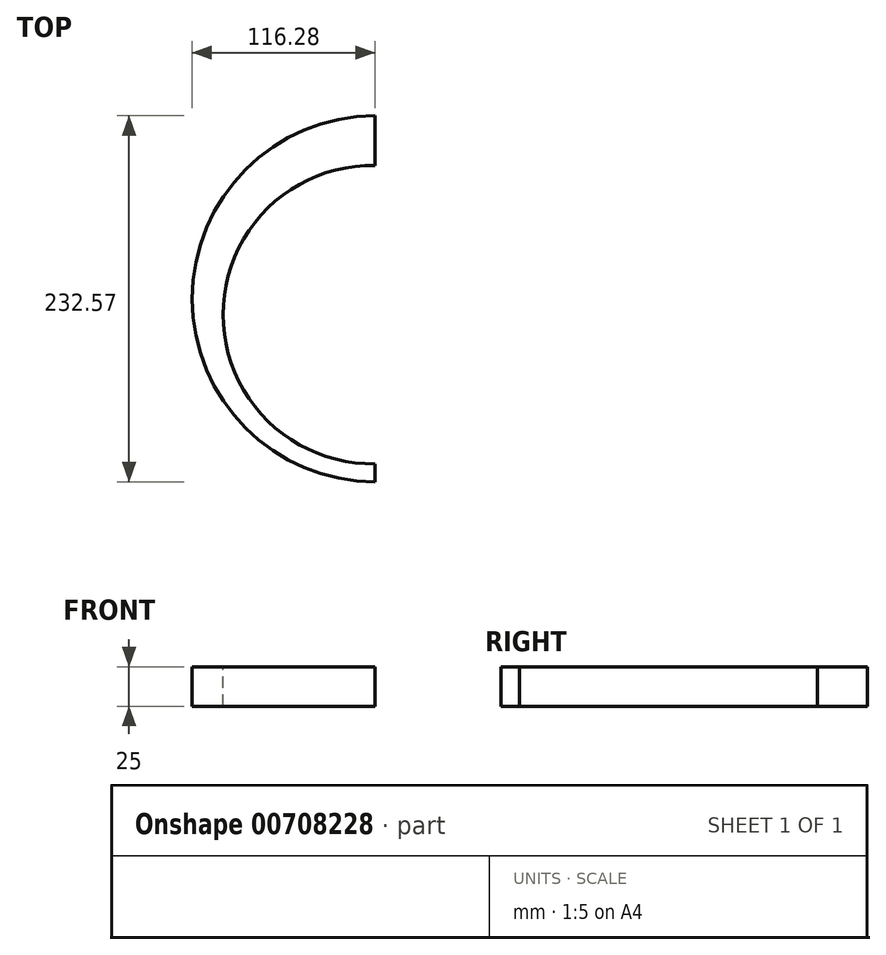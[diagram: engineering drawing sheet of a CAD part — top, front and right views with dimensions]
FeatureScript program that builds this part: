
annotation { "Feature Type Name" : "Feature", "Feature Type Description" : "" }
export const myFeature = defineFeature(function(context is Context, id is Id, definition is map)
    precondition{}
    {
        {
            var Q0;
            Q0=qCreatedBy(makeId("Top.planeOp"),FACE);
            var sketch = newSketch(context, id + "F0", { "sketchPlane" : qUnion([Q0])});
            skCircle(sketch, "E0", {"center": v(-180.25, -20.23) * mm, "radius": 116.29 * mm});
            skSolve(sketch);
        }
        {
            var Q0;
            Q0 = qSketchRegion(id + "F0", true);
            extrude(context, id + "F1", {"entities" : qUnion([Q0]), "depth" : 25 * mm, "offsetDistance" : 25 * mm});
        }
        {
            var Q0;
            Q0=makeQuery(id+"F1.opExtrude","CAP_FACE",FACE,{"disambiguationData":[OSD([sQuery(id+"F0.wireOp",EDGE,"E0")])],"isStart":false});
            var sketch = newSketch(context, id + "F2", { "sketchPlane" : qUnion([Q0])});
            skCircle(sketch, "E1", {"center": v(-182.13, -30.26) * mm, "radius": 94.76 * mm});
            skSolve(sketch);
        }
        {
            var Q0;
            Q0 = qSketchRegion(id + "F2", true);
            extrude(context, id + "F3", {"entities" : qUnion([Q0]), "operationType" : NewBodyOperationType.REMOVE, "endBound" : BoundingType.THROUGH_ALL, "oppositeDirection" : true, "depth" : 25 * mm, "offsetDistance" : 25 * mm});
        }
        {
            var Q0;
            Q0=makeQuery(id+"F1.opExtrude","CAP_FACE",FACE,{"disambiguationData":[OSD([sQuery(id+"F0.wireOp",EDGE,"E0")])],"isStart":false});
            var sketch = newSketch(context, id + "F4", { "sketchPlane" : qUnion([Q0])});
            skLineSegment(sketch, "E2", {"start": v(-180.25, -20.23) * mm, "end": v(-180.25, 124.96) * mm});
            skLineSegment(sketch, "E3", {"start": v(-180.25, 124.96) * mm, "end": v(-41.92, 124.96) * mm});
            skLineSegment(sketch, "E4", {"start": v(-41.92, 124.96) * mm, "end": v(-41.92, -167.46) * mm});
            skLineSegment(sketch, "E5", {"start": v(-41.92, -167.46) * mm, "end": v(-180.25, -167.46) * mm});
            skLineSegment(sketch, "E6", {"start": v(-180.25, -167.46) * mm, "end": v(-180.25, -20.23) * mm});
            skSolve(sketch);
        }
        {
            var Q0;
            Q0 = qSketchRegion(id + "F4", true);
            extrude(context, id + "F5", {"entities" : qUnion([Q0]), "operationType" : NewBodyOperationType.REMOVE, "endBound" : BoundingType.THROUGH_ALL, "oppositeDirection" : true, "depth" : 25 * mm, "offsetDistance" : 25 * mm});
        }
    });
